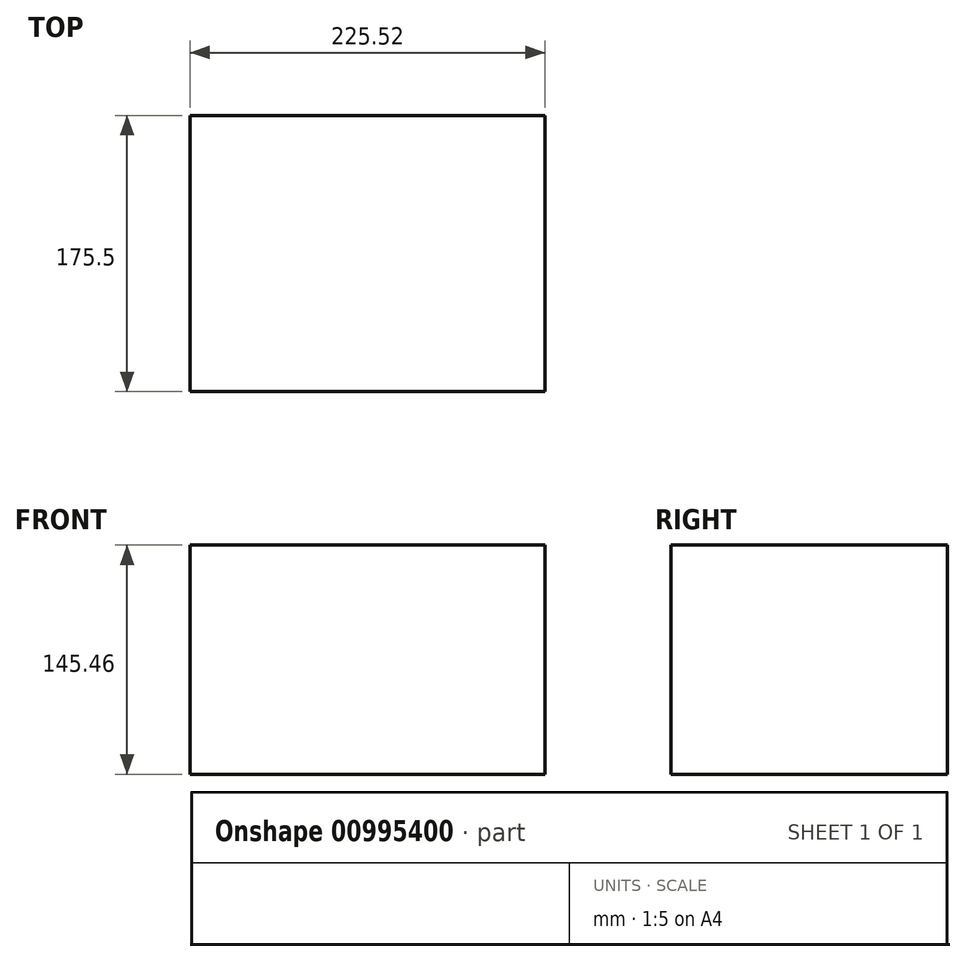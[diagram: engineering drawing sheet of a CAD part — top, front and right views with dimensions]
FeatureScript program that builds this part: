
annotation { "Feature Type Name" : "Feature", "Feature Type Description" : "" }
export const myFeature = defineFeature(function(context is Context, id is Id, definition is map)
    precondition{}
    {
        {
            var Q0;
            Q0=qCreatedBy(makeId("Front.planeOp"),FACE);
            var sketch = newSketch(context, id + "F0", { "sketchPlane" : qUnion([Q0])});
            skLineSegment(sketch, "E0.bottom", {"start": v(50.65, 56.6) * mm, "end": v(-174.87, 56.6) * mm});
            skLineSegment(sketch, "E0.top", {"start": v(50.65, -88.85) * mm, "end": v(-174.87, -88.85) * mm});
            skLineSegment(sketch, "E0.left", {"start": v(50.65, 56.6) * mm, "end": v(50.65, -88.85) * mm});
            skLineSegment(sketch, "E0.right", {"start": v(-174.87, 56.6) * mm, "end": v(-174.87, -88.85) * mm});
            skPoint(sketch, "E0.middle", {"position": v(-62.1, -16.12) * mm});
            skSolve(sketch);
        }
        {
            var Q0;
            Q0=makeQuery(id+"F0.imprint","IMPRINT",FACE,{"disambiguationData":[TD([[makeQuery(id+"F0.imprint","IMPRINT",EDGE,{"derivedFrom":sQuery(id+"F0.wireOp",EDGE,"E0.bottom")}),1.0]])]});
            extrude(context, id + "F1", {"entities" : qUnion([Q0]), "oppositeDirection" : true, "depth" : 175.5 * mm, "offsetDistance" : 25.4 * mm});
        }
    });
